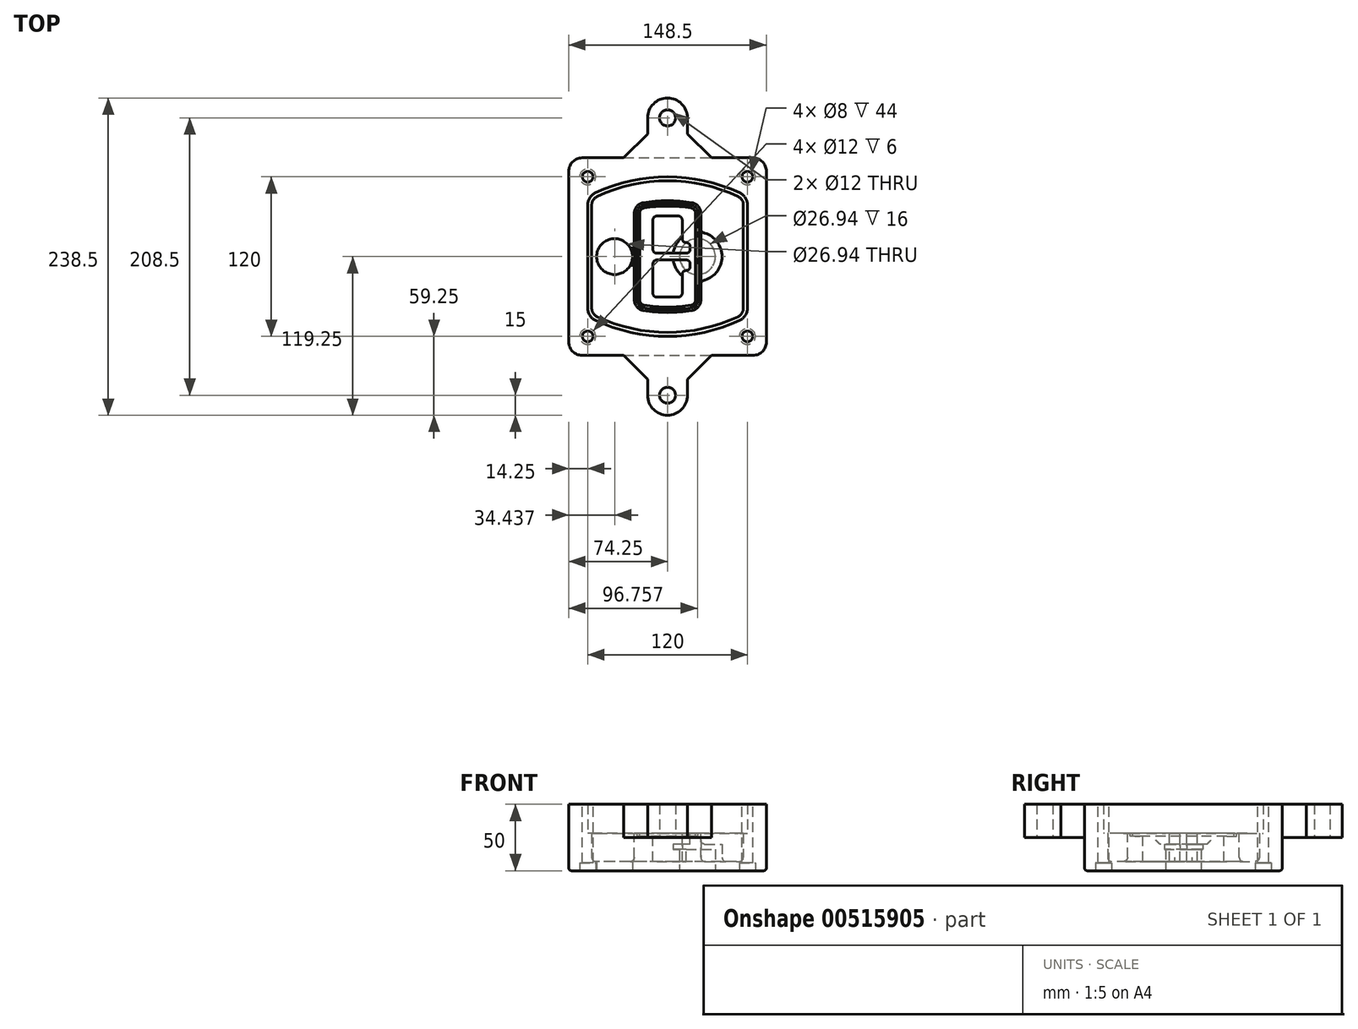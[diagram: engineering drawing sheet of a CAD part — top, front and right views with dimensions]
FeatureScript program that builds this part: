
annotation { "Feature Type Name" : "Feature", "Feature Type Description" : "" }
export const myFeature = defineFeature(function(context is Context, id is Id, definition is map)
    precondition{}
    {
        {
            var Q0;
            Q0=qCreatedBy(makeId("Top.planeOp"),FACE);
            var sketch = newSketch(context, id + "F0", { "sketchPlane" : qUnion([Q0])});
            skPoint(sketch, "E0.rect.middle", {"position": v(0, 0) * mm});
            skLineSegment(sketch, "E1.bottom", {"start": v(-64.25, -74.25) * mm, "end": v(64.25, -74.25) * mm});
            skLineSegment(sketch, "E1.top", {"start": v(-64.25, 74.25) * mm, "end": v(64.25, 74.25) * mm});
            skLineSegment(sketch, "E1.left", {"start": v(-74.25, -64.25) * mm, "end": v(-74.25, 64.25) * mm});
            skLineSegment(sketch, "E1.right", {"start": v(74.25, -64.25) * mm, "end": v(74.25, 64.25) * mm});
            skLineSegment(sketch, "E2", {"start": v(-74.25, 74.25) * mm, "end": v(74.25, -74.25) * mm, "construction": true});
            skLineSegment(sketch, "E3", {"start": v(74.25, 74.25) * mm, "end": v(-74.25, -74.25) * mm, "construction": true});
            skCircle(sketch, "E4", {"center": v(-60, 60) * mm, "radius": 4 * mm});
            skCircle(sketch, "E5", {"center": v(60, 60) * mm, "radius": 4 * mm});
            skCircle(sketch, "E6", {"center": v(60, -60) * mm, "radius": 4 * mm});
            skCircle(sketch, "E7", {"center": v(-60, -60) * mm, "radius": 4 * mm});
            skLineSegment(sketch, "E8", {"start": v(-60, 60) * mm, "end": v(60, 60) * mm, "construction": true});
            skLineSegment(sketch, "E9", {"start": v(60, 60) * mm, "end": v(60, -60) * mm, "construction": true});
            skLineSegment(sketch, "E10", {"start": v(60, -60) * mm, "end": v(-60, -60) * mm, "construction": true});
            skLineSegment(sketch, "E11", {"start": v(-60, -60) * mm, "end": v(-60, 60) * mm, "construction": true});
            skLineSegment(sketch, "E12", {"start": v(-60, 38.83) * mm, "end": v(-60, -38.83) * mm});
            skLineSegment(sketch, "E13", {"start": v(60, 38.83) * mm, "end": v(60, -38.83) * mm});
            skArc(sketch, "E14", {"start": v(54.26, 47.88) * mm, "mid": v(0, 60) * mm, "end": v(-54.26, 47.88) * mm});
            skArc(sketch, "E15", {"start": v(-54.26, -47.88) * mm, "mid": v(0, -60) * mm, "end": v(54.26, -47.88) * mm});
            skLineSegment(sketch, "E16", {"start": v(-60, 0) * mm, "end": v(60, 0) * mm, "construction": true});
            skPoint(sketch, "E17.visualSharp", {"position": v(-60, -45) * mm});
            skArc(sketch, "E17.filletArc", {"start": v(-60, -38.83) * mm, "mid": v(-58.44, -44.2) * mm, "end": v(-54.26, -47.88) * mm});
            skPoint(sketch, "E18.visualSharp", {"position": v(-60, 45) * mm});
            skArc(sketch, "E18.filletArc", {"start": v(-54.26, 47.88) * mm, "mid": v(-58.44, 44.2) * mm, "end": v(-60, 38.83) * mm});
            skPoint(sketch, "E19.visualSharp", {"position": v(60, 45) * mm});
            skArc(sketch, "E19.filletArc", {"start": v(60, 38.83) * mm, "mid": v(58.44, 44.2) * mm, "end": v(54.26, 47.88) * mm});
            skPoint(sketch, "E20.visualSharp", {"position": v(60, -45) * mm});
            skArc(sketch, "E20.filletArc", {"start": v(54.26, -47.88) * mm, "mid": v(58.44, -44.2) * mm, "end": v(60, -38.83) * mm});
            skPoint(sketch, "E21.visualSharp", {"position": v(-74.25, 74.25) * mm});
            skArc(sketch, "E21.filletArc", {"start": v(-64.25, 74.25) * mm, "mid": v(-71.32, 71.32) * mm, "end": v(-74.25, 64.25) * mm});
            skPoint(sketch, "E22.visualSharp", {"position": v(74.25, 74.25) * mm});
            skArc(sketch, "E22.filletArc", {"start": v(74.25, 64.25) * mm, "mid": v(71.32, 71.32) * mm, "end": v(64.25, 74.25) * mm});
            skPoint(sketch, "E23.visualSharp", {"position": v(74.25, -74.25) * mm});
            skArc(sketch, "E23.filletArc", {"start": v(64.25, -74.25) * mm, "mid": v(71.32, -71.32) * mm, "end": v(74.25, -64.25) * mm});
            skPoint(sketch, "E24.visualSharp", {"position": v(-74.25, -74.25) * mm});
            skArc(sketch, "E24.filletArc", {"start": v(-74.25, -64.25) * mm, "mid": v(-71.32, -71.32) * mm, "end": v(-64.25, -74.25) * mm});
            skArc(sketch, "E25.0", {"start": v(57, 38.83) * mm, "mid": v(55.9, 42.58) * mm, "end": v(52.98, 45.17) * mm});
            skLineSegment(sketch, "E25.1", {"start": v(57, 38.83) * mm, "end": v(57, -38.83) * mm});
            skArc(sketch, "E25.2", {"start": v(52.98, -45.17) * mm, "mid": v(55.9, -42.58) * mm, "end": v(57, -38.83) * mm});
            skArc(sketch, "E25.3", {"start": v(-52.98, -45.17) * mm, "mid": v(0, -57) * mm, "end": v(52.98, -45.17) * mm});
            skArc(sketch, "E25.4", {"start": v(-57, -38.83) * mm, "mid": v(-55.9, -42.58) * mm, "end": v(-52.98, -45.17) * mm});
            skArc(sketch, "E25.5", {"start": v(52.98, 45.17) * mm, "mid": v(0, 57) * mm, "end": v(-52.98, 45.17) * mm});
            skLineSegment(sketch, "E25.6", {"start": v(-57, 38.83) * mm, "end": v(-57, -38.83) * mm});
            skArc(sketch, "E25.7", {"start": v(-52.98, 45.17) * mm, "mid": v(-55.9, 42.58) * mm, "end": v(-57, 38.83) * mm});
            skArc(sketch, "E26.0", {"start": v(-55.96, 51.5) * mm, "mid": v(-61.82, 46.33) * mm, "end": v(-64, 38.83) * mm});
            skArc(sketch, "E26.1", {"start": v(55.96, 51.5) * mm, "mid": v(0, 64) * mm, "end": v(-55.96, 51.5) * mm});
            skArc(sketch, "E26.2", {"start": v(64, 38.83) * mm, "mid": v(61.82, 46.33) * mm, "end": v(55.96, 51.5) * mm});
            skLineSegment(sketch, "E26.3", {"start": v(64, 38.83) * mm, "end": v(64, -38.83) * mm});
            skArc(sketch, "E26.4", {"start": v(55.96, -51.5) * mm, "mid": v(61.82, -46.33) * mm, "end": v(64, -38.83) * mm});
            skLineSegment(sketch, "E26.5", {"start": v(-64, 38.83) * mm, "end": v(-64, -38.83) * mm});
            skArc(sketch, "E26.6", {"start": v(-55.96, -51.5) * mm, "mid": v(0, -64) * mm, "end": v(55.96, -51.5) * mm});
            skArc(sketch, "E26.7", {"start": v(-64, -38.83) * mm, "mid": v(-61.82, -46.33) * mm, "end": v(-55.96, -51.5) * mm});
            skSolve(sketch);
        }
        {
            var Q0;
            Q0=makeQuery(id+"F0.imprint","IMPRINT",FACE,{"disambiguationData":[TD([[makeQuery(id+"F0.imprint","IMPRINT",EDGE,{"derivedFrom":sQuery(id+"F0.wireOp",EDGE,"E1.bottom")}),1.0]])]});
            var Q1;
            Q1=makeQuery(id+"F0.imprint","IMPRINT",FACE,{"disambiguationData":[TD([[makeQuery(id+"F0.imprint","IMPRINT",EDGE,{"derivedFrom":sQuery(id+"F0.wireOp",EDGE,"E12")}),1.0]])]});
            var Q2;
            Q2=makeQuery(id+"F0.imprint","IMPRINT",FACE,{"disambiguationData":[TD([[makeQuery(id+"F0.imprint","IMPRINT",EDGE,{"derivedFrom":sQuery(id+"F0.wireOp",EDGE,"E25.0")}),1.0]])]});
            var Q3;
            Q3=makeQuery(id+"F0.imprint","IMPRINT",FACE,{"disambiguationData":[TD([[makeQuery(id+"F0.imprint","IMPRINT",EDGE,{"derivedFrom":sQuery(id+"F0.wireOp",EDGE,"E12")}),-1.0]])]});
            extrude(context, id + "F1", {"entities" : qUnion([Q0, Q1, Q2, Q3]), "oppositeDirection" : true, "depth" : 25 * mm});
        }
        {
            var Q0;
            Q0=makeQuery(id+"F0.imprint","IMPRINT",FACE,{"disambiguationData":[TD([[makeQuery(id+"F0.imprint","IMPRINT",EDGE,{"derivedFrom":sQuery(id+"F0.wireOp",EDGE,"E12")}),1.0]])]});
            extrude(context, id + "F2", {"entities" : qUnion([Q0]), "operationType" : NewBodyOperationType.ADD, "depth" : 3 * mm});
        }
        {
            var Q0;
            Q0=makeQuery(id+"F0.imprint","IMPRINT",FACE,{"disambiguationData":[TD([[makeQuery(id+"F0.imprint","IMPRINT",EDGE,{"derivedFrom":sQuery(id+"F0.wireOp",EDGE,"E25.0")}),1.0]])]});
            extrude(context, id + "F3", {"entities" : qUnion([Q0]), "operationType" : NewBodyOperationType.REMOVE, "oppositeDirection" : true, "depth" : 18 * mm});
        }
        {
            var Q0;
            Q0=makeQuery(id+"F2.opExtrude","CAP_FACE",FACE,{"disambiguationData":[OSD([sQuery(id+"F0.wireOp",EDGE,"E12"),sQuery(id+"F0.wireOp",EDGE,"E13"),sQuery(id+"F0.wireOp",EDGE,"E14"),sQuery(id+"F0.wireOp",EDGE,"E15"),sQuery(id+"F0.wireOp",EDGE,"E17.filletArc"),sQuery(id+"F0.wireOp",EDGE,"E18.filletArc"),sQuery(id+"F0.wireOp",EDGE,"E19.filletArc"),sQuery(id+"F0.wireOp",EDGE,"E20.filletArc"),sQuery(id+"F0.wireOp",EDGE,"E25.0"),sQuery(id+"F0.wireOp",EDGE,"E25.1"),sQuery(id+"F0.wireOp",EDGE,"E25.2"),sQuery(id+"F0.wireOp",EDGE,"E25.3"),sQuery(id+"F0.wireOp",EDGE,"E25.4"),sQuery(id+"F0.wireOp",EDGE,"E25.5"),sQuery(id+"F0.wireOp",EDGE,"E25.6"),sQuery(id+"F0.wireOp",EDGE,"E25.7")])],"isStart":false});
            var sketch = newSketch(context, id + "F4", { "sketchPlane" : qUnion([Q0])});
            skArc(sketch, "E27.0", {"start": v(-18.34, -40.45) * mm, "mid": v(0, -42) * mm, "end": v(18.34, -40.45) * mm});
            skArc(sketch, "E28.0", {"start": v(18.34, 40.45) * mm, "mid": v(0, 42) * mm, "end": v(-18.34, 40.45) * mm});
            skLineSegment(sketch, "E29", {"start": v(-25, 32.57) * mm, "end": v(-25, -32.57) * mm});
            skLineSegment(sketch, "E30", {"start": v(25, 32.57) * mm, "end": v(25, -32.57) * mm});
            skLineSegment(sketch, "E31", {"start": v(-25, 39.1) * mm, "end": v(25, 39.1) * mm, "construction": true});
            skLineSegment(sketch, "E32", {"start": v(-25, -39.1) * mm, "end": v(25, -39.1) * mm, "construction": true});
            skPoint(sketch, "E33.visualSharp", {"position": v(-25, 39.1) * mm});
            skArc(sketch, "E33.filletArc", {"start": v(-18.34, 40.45) * mm, "mid": v(-23.11, 37.73) * mm, "end": v(-25, 32.57) * mm});
            skPoint(sketch, "E34.visualSharp", {"position": v(25, 39.1) * mm});
            skArc(sketch, "E34.filletArc", {"start": v(25, 32.57) * mm, "mid": v(23.11, 37.73) * mm, "end": v(18.34, 40.45) * mm});
            skPoint(sketch, "E35.visualSharp", {"position": v(25, -39.1) * mm});
            skArc(sketch, "E35.filletArc", {"start": v(18.34, -40.45) * mm, "mid": v(23.11, -37.73) * mm, "end": v(25, -32.57) * mm});
            skPoint(sketch, "E36.visualSharp", {"position": v(-25, -39.1) * mm});
            skArc(sketch, "E36.filletArc", {"start": v(-25, -32.57) * mm, "mid": v(-23.11, -37.73) * mm, "end": v(-18.34, -40.45) * mm});
            skArc(sketch, "E37.0", {"start": v(52.98, 45.17) * mm, "mid": v(0, 57) * mm, "end": v(-52.98, 45.17) * mm});
            skArc(sketch, "E37.1", {"start": v(-52.98, 45.17) * mm, "mid": v(-55.9, 42.58) * mm, "end": v(-57, 38.83) * mm});
            skLineSegment(sketch, "E37.2", {"start": v(-57, 38.83) * mm, "end": v(-57, -38.83) * mm});
            skArc(sketch, "E37.3", {"start": v(-57, -38.83) * mm, "mid": v(-55.9, -42.58) * mm, "end": v(-52.98, -45.17) * mm});
            skArc(sketch, "E37.4", {"start": v(-52.98, -45.17) * mm, "mid": v(0, -57) * mm, "end": v(52.98, -45.17) * mm});
            skArc(sketch, "E37.5", {"start": v(52.98, -45.17) * mm, "mid": v(55.9, -42.58) * mm, "end": v(57, -38.83) * mm});
            skLineSegment(sketch, "E37.6", {"start": v(57, 38.83) * mm, "end": v(57, -38.83) * mm});
            skArc(sketch, "E37.7", {"start": v(57, 38.83) * mm, "mid": v(55.9, 42.58) * mm, "end": v(52.98, 45.17) * mm});
            skLineSegment(sketch, "E38.0", {"start": v(23, 32.57) * mm, "end": v(23, -32.57) * mm});
            skArc(sketch, "E38.1", {"start": v(18, -38.48) * mm, "mid": v(21.58, -36.44) * mm, "end": v(23, -32.57) * mm});
            skArc(sketch, "E38.2", {"start": v(-18, -38.48) * mm, "mid": v(0, -40) * mm, "end": v(18, -38.48) * mm});
            skArc(sketch, "E38.3", {"start": v(-23, -32.57) * mm, "mid": v(-21.58, -36.44) * mm, "end": v(-18, -38.48) * mm});
            skLineSegment(sketch, "E38.4", {"start": v(-23, 32.57) * mm, "end": v(-23, -32.57) * mm});
            skArc(sketch, "E38.5", {"start": v(23, 32.57) * mm, "mid": v(21.58, 36.44) * mm, "end": v(18, 38.48) * mm});
            skArc(sketch, "E38.6", {"start": v(-18, 38.48) * mm, "mid": v(-21.58, 36.44) * mm, "end": v(-23, 32.57) * mm});
            skArc(sketch, "E38.7", {"start": v(18, 38.48) * mm, "mid": v(0, 40) * mm, "end": v(-18, 38.48) * mm});
            skArc(sketch, "E39.0", {"start": v(21, 32.57) * mm, "mid": v(20.06, 35.15) * mm, "end": v(17.67, 36.5) * mm});
            skLineSegment(sketch, "E39.1", {"start": v(21, 32.57) * mm, "end": v(21, -32.57) * mm});
            skArc(sketch, "E39.2", {"start": v(17.67, -36.5) * mm, "mid": v(20.06, -35.15) * mm, "end": v(21, -32.57) * mm});
            skArc(sketch, "E39.3", {"start": v(-17.67, -36.5) * mm, "mid": v(0, -38) * mm, "end": v(17.67, -36.5) * mm});
            skArc(sketch, "E39.4", {"start": v(-21, -32.57) * mm, "mid": v(-20.06, -35.15) * mm, "end": v(-17.67, -36.5) * mm});
            skArc(sketch, "E39.5", {"start": v(17.67, 36.5) * mm, "mid": v(0, 38) * mm, "end": v(-17.67, 36.5) * mm});
            skLineSegment(sketch, "E39.6", {"start": v(-21, 32.57) * mm, "end": v(-21, -32.57) * mm});
            skArc(sketch, "E39.7", {"start": v(-17.67, 36.5) * mm, "mid": v(-20.06, 35.15) * mm, "end": v(-21, 32.57) * mm});
            skLineSegment(sketch, "E40", {"start": v(-25, 0) * mm, "end": v(25, 0) * mm, "construction": true});
            skLineSegment(sketch, "E41", {"start": v(-11, 5.5) * mm, "end": v(-11, 27.5) * mm});
            skLineSegment(sketch, "E42", {"start": v(-8, 30.5) * mm, "end": v(8, 30.5) * mm});
            skLineSegment(sketch, "E43", {"start": v(11, 27.5) * mm, "end": v(11, 13.5) * mm});
            skLineSegment(sketch, "E44", {"start": v(14, 10.5) * mm, "end": v(14, 10.5) * mm});
            skLineSegment(sketch, "E45", {"start": v(17, 7.5) * mm, "end": v(17, 5.5) * mm});
            skLineSegment(sketch, "E46", {"start": v(14, 2.5) * mm, "end": v(-8, 2.5) * mm});
            skPoint(sketch, "E47.visualSharp", {"position": v(-11, 30.5) * mm});
            skArc(sketch, "E47.filletArc", {"start": v(-8, 30.5) * mm, "mid": v(-10.12, 29.62) * mm, "end": v(-11, 27.5) * mm});
            skPoint(sketch, "E48.visualSharp", {"position": v(11, 30.5) * mm});
            skArc(sketch, "E48.filletArc", {"start": v(11, 27.5) * mm, "mid": v(10.12, 29.62) * mm, "end": v(8, 30.5) * mm});
            skPoint(sketch, "E49.visualSharp", {"position": v(11, 10.5) * mm});
            skArc(sketch, "E49.filletArc", {"start": v(11, 13.5) * mm, "mid": v(11.88, 11.38) * mm, "end": v(14, 10.5) * mm});
            skPoint(sketch, "E50.visualSharp", {"position": v(17, 10.5) * mm});
            skArc(sketch, "E50.filletArc", {"start": v(17, 7.5) * mm, "mid": v(16.12, 9.62) * mm, "end": v(14, 10.5) * mm});
            skPoint(sketch, "E51.visualSharp", {"position": v(17, 2.5) * mm});
            skArc(sketch, "E51.filletArc", {"start": v(14, 2.5) * mm, "mid": v(16.12, 3.38) * mm, "end": v(17, 5.5) * mm});
            skPoint(sketch, "E52.visualSharp", {"position": v(-11, 2.5) * mm});
            skArc(sketch, "E52.filletArc", {"start": v(-11, 5.5) * mm, "mid": v(-10.12, 3.38) * mm, "end": v(-8, 2.5) * mm});
            skLineSegment(sketch, "E53.0.MirrorCS", {"start": v(14, -2.5) * mm, "end": v(-8, -2.5) * mm});
            skArc(sketch, "E54.0.MirrorCS", {"start": v(-11, -5.5) * mm, "mid": v(-10.12, -3.38) * mm, "end": v(-8, -2.5) * mm});
            skLineSegment(sketch, "E55.0.MirrorCS", {"start": v(-11, -5.5) * mm, "end": v(-11, -27.5) * mm});
            skArc(sketch, "E56.0.MirrorCS", {"start": v(-8, -30.5) * mm, "mid": v(-10.12, -29.62) * mm, "end": v(-11, -27.5) * mm});
            skLineSegment(sketch, "E57.0.MirrorCS", {"start": v(-8, -30.5) * mm, "end": v(8, -30.5) * mm});
            skArc(sketch, "E58.0.MirrorCS", {"start": v(11, -27.5) * mm, "mid": v(10.12, -29.62) * mm, "end": v(8, -30.5) * mm});
            skLineSegment(sketch, "E59.0.MirrorCS", {"start": v(11, -27.5) * mm, "end": v(11, -13.5) * mm});
            skArc(sketch, "E60.0.MirrorCS", {"start": v(11, -13.5) * mm, "mid": v(11.88, -11.38) * mm, "end": v(14, -10.5) * mm});
            skArc(sketch, "E61.0.MirrorCS", {"start": v(17, -7.5) * mm, "mid": v(16.12, -9.62) * mm, "end": v(14, -10.5) * mm});
            skLineSegment(sketch, "E62.0.MirrorCS", {"start": v(17, -7.5) * mm, "end": v(17, -5.5) * mm});
            skArc(sketch, "E63.0.MirrorCS", {"start": v(14, -2.5) * mm, "mid": v(16.12, -3.38) * mm, "end": v(17, -5.5) * mm});
            skSolve(sketch);
        }
        {
            var Q0;
            Q0=makeQuery(id+"F4.imprint","IMPRINT",FACE,{"disambiguationData":[TD([[makeQuery(id+"F4.imprint","IMPRINT",EDGE,{"derivedFrom":sQuery(id+"F4.wireOp",EDGE,"E27.0")}),1.0]])]});
            var Q1;
            Q1=makeQuery(id+"F4.imprint","IMPRINT",FACE,{"disambiguationData":[TD([[makeQuery(id+"F4.imprint","IMPRINT",EDGE,{"derivedFrom":sQuery(id+"F4.wireOp",EDGE,"E38.0")}),-1.0]])]});
            var Q2;
            Q2=makeQuery(id+"F4.imprint","IMPRINT",FACE,{"disambiguationData":[TD([[makeQuery(id+"F4.imprint","IMPRINT",EDGE,{"derivedFrom":sQuery(id+"F4.wireOp",EDGE,"E39.0")}),1.0]])]});
            extrude(context, id + "F5", {"entities" : qUnion([Q0, Q1, Q2]), "operationType" : NewBodyOperationType.ADD, "endBound" : BoundingType.UP_TO_NEXT, "oppositeDirection" : true, "depth" : 25 * mm});
        }
        {
            var Q0;
            Q0=makeQuery(id+"F4.imprint","IMPRINT",FACE,{"disambiguationData":[TD([[makeQuery(id+"F4.imprint","IMPRINT",EDGE,{"derivedFrom":sQuery(id+"F4.wireOp",EDGE,"E38.0")}),-1.0]])]});
            extrude(context, id + "F6", {"entities" : qUnion([Q0]), "operationType" : NewBodyOperationType.REMOVE, "oppositeDirection" : true, "depth" : 2 * mm});
        }
        {
            var Q0;
            Q0=makeQuery(id+"F1.opExtrude","CAP_FACE",FACE,{"disambiguationData":[OSD([sQuery(id+"F0.wireOp",EDGE,"E1.bottom"),sQuery(id+"F0.wireOp",EDGE,"E1.top"),sQuery(id+"F0.wireOp",EDGE,"E1.left"),sQuery(id+"F0.wireOp",EDGE,"E1.right"),sQuery(id+"F0.wireOp",EDGE,"E4"),sQuery(id+"F0.wireOp",EDGE,"E5"),sQuery(id+"F0.wireOp",EDGE,"E6"),sQuery(id+"F0.wireOp",EDGE,"E7"),sQuery(id+"F0.wireOp",EDGE,"E21.filletArc"),sQuery(id+"F0.wireOp",EDGE,"E22.filletArc"),sQuery(id+"F0.wireOp",EDGE,"E23.filletArc"),sQuery(id+"F0.wireOp",EDGE,"E24.filletArc")])],"isStart":false});
            var sketch = newSketch(context, id + "F7", { "sketchPlane" : qUnion([Q0])});
            skCircle(sketch, "E64", {"center": v(22.5, 0) * mm, "radius": 13.47 * mm});
            skCircle(sketch, "E65", {"center": v(-39.81, 0) * mm, "radius": 13.47 * mm});
            skLineSegment(sketch, "E66", {"start": v(74.25, 0) * mm, "end": v(-74.25, 0) * mm});
            skCircle(sketch, "E67", {"center": v(22.5, 0) * mm, "radius": 18.47 * mm});
            skCircle(sketch, "E68", {"center": v(60, -60) * mm, "radius": 6 * mm});
            skCircle(sketch, "E69", {"center": v(-60, -60) * mm, "radius": 6 * mm});
            skCircle(sketch, "E70", {"center": v(-60, 60) * mm, "radius": 6 * mm});
            skCircle(sketch, "E71", {"center": v(60, 60) * mm, "radius": 6 * mm});
            skSolve(sketch);
        }
        {
            var Q0;
            {var subQ1=sQuery(id+"F7.wireOp",EDGE,"E66");var subQ4=sQuery(id+"F7.wireOp",EDGE,"E64");var subQ6=makeQuery(id+"F7.imprint","INTERSECT",VERTEX,{"disambiguationData":[OD(0.0)],"derivedFrom":[subQ4,subQ1]});Q0=makeQuery(id+"F7.imprint","IMPRINT",FACE,{"disambiguationData":[TD([[makeQuery(id+"F7.imprint","IMPRINT",EDGE,{"disambiguationData":[TD([[subQ6,-1.0]])],"derivedFrom":subQ4}),-1.0]])]});}
            var Q1;
            {var subQ0=sQuery(id+"F7.wireOp",EDGE,"E66");var subQ1=sQuery(id+"F7.wireOp",EDGE,"E64");var subQ3=makeQuery(id+"F7.imprint","INTERSECT",VERTEX,{"disambiguationData":[OD(0.0)],"derivedFrom":[subQ1,subQ0]});Q1=makeQuery(id+"F7.imprint","IMPRINT",FACE,{"disambiguationData":[TD([[makeQuery(id+"F7.imprint","IMPRINT",EDGE,{"disambiguationData":[TD([[subQ3,-1.0]])],"derivedFrom":subQ1}),1.0]])]});}
            var Q2;
            {var subQ0=sQuery(id+"F7.wireOp",EDGE,"E66");var subQ1=sQuery(id+"F7.wireOp",EDGE,"E64");var subQ3=makeQuery(id+"F7.imprint","INTERSECT",VERTEX,{"disambiguationData":[OD(0.0)],"derivedFrom":[subQ1,subQ0]});Q2=makeQuery(id+"F7.imprint","IMPRINT",FACE,{"disambiguationData":[TD([[makeQuery(id+"F7.imprint","IMPRINT",EDGE,{"disambiguationData":[TD([[subQ3,1.0]])],"derivedFrom":subQ1}),1.0]])]});}
            var Q3;
            {var subQ1=sQuery(id+"F7.wireOp",EDGE,"E66");var subQ4=sQuery(id+"F7.wireOp",EDGE,"E64");var subQ6=makeQuery(id+"F7.imprint","INTERSECT",VERTEX,{"disambiguationData":[OD(0.0)],"derivedFrom":[subQ4,subQ1]});Q3=makeQuery(id+"F7.imprint","IMPRINT",FACE,{"disambiguationData":[TD([[makeQuery(id+"F7.imprint","IMPRINT",EDGE,{"disambiguationData":[TD([[subQ6,1.0]])],"derivedFrom":subQ4}),-1.0]])]});}
            extrude(context, id + "F8", {"entities" : qUnion([Q0, Q1, Q2, Q3]), "operationType" : NewBodyOperationType.ADD, "oppositeDirection" : true, "depth" : 20 * mm});
        }
        {
            var Q0;
            {var subQ0=sQuery(id+"F7.wireOp",EDGE,"E66");var subQ1=sQuery(id+"F7.wireOp",EDGE,"E64");var subQ3=makeQuery(id+"F7.imprint","INTERSECT",VERTEX,{"disambiguationData":[OD(0.0)],"derivedFrom":[subQ1,subQ0]});Q0=makeQuery(id+"F7.imprint","IMPRINT",FACE,{"disambiguationData":[TD([[makeQuery(id+"F7.imprint","IMPRINT",EDGE,{"disambiguationData":[TD([[subQ3,-1.0]])],"derivedFrom":subQ1}),1.0]])]});}
            var Q1;
            {var subQ0=sQuery(id+"F7.wireOp",EDGE,"E66");var subQ1=sQuery(id+"F7.wireOp",EDGE,"E64");var subQ3=makeQuery(id+"F7.imprint","INTERSECT",VERTEX,{"disambiguationData":[OD(0.0)],"derivedFrom":[subQ1,subQ0]});Q1=makeQuery(id+"F7.imprint","IMPRINT",FACE,{"disambiguationData":[TD([[makeQuery(id+"F7.imprint","IMPRINT",EDGE,{"disambiguationData":[TD([[subQ3,1.0]])],"derivedFrom":subQ1}),1.0]])]});}
            extrude(context, id + "F9", {"entities" : qUnion([Q0, Q1]), "operationType" : NewBodyOperationType.REMOVE, "oppositeDirection" : true, "depth" : 16 * mm});
        }
        {
            var Q0;
            {var subQ0=sQuery(id+"F7.wireOp",EDGE,"E66");var subQ1=sQuery(id+"F7.wireOp",EDGE,"E65");var subQ3=makeQuery(id+"F7.imprint","INTERSECT",VERTEX,{"disambiguationData":[OD(0.0)],"derivedFrom":[subQ1,subQ0]});Q0=makeQuery(id+"F7.imprint","IMPRINT",FACE,{"disambiguationData":[TD([[makeQuery(id+"F7.imprint","IMPRINT",EDGE,{"disambiguationData":[TD([[subQ3,-1.0]])],"derivedFrom":subQ1}),1.0]])]});}
            var Q1;
            {var subQ0=sQuery(id+"F7.wireOp",EDGE,"E66");var subQ1=sQuery(id+"F7.wireOp",EDGE,"E65");var subQ3=makeQuery(id+"F7.imprint","INTERSECT",VERTEX,{"disambiguationData":[OD(0.0)],"derivedFrom":[subQ1,subQ0]});Q1=makeQuery(id+"F7.imprint","IMPRINT",FACE,{"disambiguationData":[TD([[makeQuery(id+"F7.imprint","IMPRINT",EDGE,{"disambiguationData":[TD([[subQ3,1.0]])],"derivedFrom":subQ1}),1.0]])]});}
            extrude(context, id + "F10", {"entities" : qUnion([Q0, Q1]), "operationType" : NewBodyOperationType.REMOVE, "oppositeDirection" : true, "depth" : 25 * mm});
        }
        {
            var Q0;
            Q0=makeQuery(id+"F7.imprint","IMPRINT",FACE,{"disambiguationData":[TD([[makeQuery(id+"F7.imprint","IMPRINT",EDGE,{"derivedFrom":sQuery(id+"F7.wireOp",EDGE,"E68")}),1.0]])]});
            var Q1;
            Q1=makeQuery(id+"F7.imprint","IMPRINT",FACE,{"disambiguationData":[TD([[makeQuery(id+"F7.imprint","IMPRINT",EDGE,{"derivedFrom":makeQuery(id+"F1.opExtrude","CAP_EDGE",EDGE,{"disambiguationData":[OSD([sQuery(id+"F0.wireOp",EDGE,"E5")])],"isStart":false})}),-1.0]])]});
            var Q2;
            Q2=makeQuery(id+"F7.imprint","IMPRINT",FACE,{"disambiguationData":[TD([[makeQuery(id+"F7.imprint","IMPRINT",EDGE,{"derivedFrom":sQuery(id+"F7.wireOp",EDGE,"E69")}),1.0]])]});
            var Q3;
            Q3=makeQuery(id+"F7.imprint","IMPRINT",FACE,{"disambiguationData":[TD([[makeQuery(id+"F7.imprint","IMPRINT",EDGE,{"derivedFrom":makeQuery(id+"F1.opExtrude","CAP_EDGE",EDGE,{"disambiguationData":[OSD([sQuery(id+"F0.wireOp",EDGE,"E4")])],"isStart":false})}),-1.0]])]});
            var Q4;
            Q4=makeQuery(id+"F7.imprint","IMPRINT",FACE,{"disambiguationData":[TD([[makeQuery(id+"F7.imprint","IMPRINT",EDGE,{"derivedFrom":sQuery(id+"F7.wireOp",EDGE,"E70")}),1.0]])]});
            var Q5;
            Q5=makeQuery(id+"F7.imprint","IMPRINT",FACE,{"disambiguationData":[TD([[makeQuery(id+"F7.imprint","IMPRINT",EDGE,{"derivedFrom":makeQuery(id+"F1.opExtrude","CAP_EDGE",EDGE,{"disambiguationData":[OSD([sQuery(id+"F0.wireOp",EDGE,"E7")])],"isStart":false})}),-1.0]])]});
            var Q6;
            Q6=makeQuery(id+"F7.imprint","IMPRINT",FACE,{"disambiguationData":[TD([[makeQuery(id+"F7.imprint","IMPRINT",EDGE,{"derivedFrom":sQuery(id+"F7.wireOp",EDGE,"E71")}),1.0]])]});
            var Q7;
            Q7=makeQuery(id+"F7.imprint","IMPRINT",FACE,{"disambiguationData":[TD([[makeQuery(id+"F7.imprint","IMPRINT",EDGE,{"derivedFrom":makeQuery(id+"F1.opExtrude","CAP_EDGE",EDGE,{"disambiguationData":[OSD([sQuery(id+"F0.wireOp",EDGE,"E6")])],"isStart":false})}),-1.0]])]});
            extrude(context, id + "F11", {"entities" : qUnion([Q0, Q1, Q2, Q3, Q4, Q5, Q6, Q7]), "operationType" : NewBodyOperationType.REMOVE, "oppositeDirection" : true, "depth" : 6 * mm});
        }
        {
            var Q0;
            Q0=makeQuery(id+"F9.boolean.opBoolean","COPY",FACE,{"derivedFrom":makeQuery(id+"F9.opExtrude","CAP_FACE",FACE,{"disambiguationData":[OSD([sQuery(id+"F7.wireOp",EDGE,"E64")])],"isStart":false})});
            var sketch = newSketch(context, id + "F12", { "sketchPlane" : qUnion([Q0])});
            skArc(sketch, "E72.0", {"start": v(11, 14.45) * mm, "mid": v(6.45, 9.13) * mm, "end": v(4.2, 2.5) * mm});
            skArc(sketch, "E72.1", {"start": v(4.2, -2.5) * mm, "mid": v(6.45, -9.13) * mm, "end": v(11, -14.45) * mm});
            skLineSegment(sketch, "E73", {"start": v(4.2, -2.5) * mm, "end": v(14, -2.5) * mm});
            skLineSegment(sketch, "E74.0", {"start": v(14, 2.5) * mm, "end": v(4.2, 2.5) * mm});
            skArc(sketch, "E74.1", {"start": v(14, 2.5) * mm, "mid": v(16.12, 3.38) * mm, "end": v(17, 5.5) * mm});
            skLineSegment(sketch, "E74.2", {"start": v(17, 7.5) * mm, "end": v(17, 5.5) * mm});
            skArc(sketch, "E74.3", {"start": v(17, 7.5) * mm, "mid": v(16.12, 9.62) * mm, "end": v(14, 10.5) * mm});
            skArc(sketch, "E74.4", {"start": v(11, 13.5) * mm, "mid": v(11.88, 11.38) * mm, "end": v(14, 10.5) * mm});
            skLineSegment(sketch, "E74.5", {"start": v(11, 14.45) * mm, "end": v(11, 13.5) * mm});
            skLineSegment(sketch, "E74.7", {"start": v(14, -2.5) * mm, "end": v(4.2, -2.5) * mm});
            skArc(sketch, "E74.8", {"start": v(14, -2.5) * mm, "mid": v(16.12, -3.38) * mm, "end": v(17, -5.5) * mm});
            skLineSegment(sketch, "E74.9", {"start": v(17, -7.5) * mm, "end": v(17, -5.5) * mm});
            skArc(sketch, "E74.10", {"start": v(17, -7.5) * mm, "mid": v(16.12, -9.62) * mm, "end": v(14, -10.5) * mm});
            skArc(sketch, "E74.11", {"start": v(11, -13.5) * mm, "mid": v(11.88, -11.38) * mm, "end": v(14, -10.5) * mm});
            skLineSegment(sketch, "E74.12", {"start": v(11, -14.45) * mm, "end": v(11, -13.5) * mm});
            skPoint(sketch, "E75.orphan", {"position": v(11, -27.5) * mm});
            skPoint(sketch, "E76.orphan", {"position": v(-8, -2.5) * mm});
            skPoint(sketch, "E77.orphan", {"position": v(-8, 2.5) * mm});
            skPoint(sketch, "E78.orphan", {"position": v(11, 27.5) * mm});
            skSolve(sketch);
        }
        {
            var Q0;
            {var subQ7=sQuery(id+"F12.wireOp",EDGE,"E72.0");var subQ14=sQuery(id+"F12.wireOp",EDGE,"E72.1");var subQ16=sQuery(id+"F12.wireOp",EDGE,"E74.1");var subQ18=sQuery(id+"F12.wireOp",EDGE,"E74.8");Q0=qUnion([makeQuery(id+"F12.imprint","IMPRINT",FACE,{"disambiguationData":[TD([[makeQuery(id+"F12.imprint","IMPRINT",EDGE,{"derivedFrom":subQ7}),1.0]])]}),makeQuery(id+"F12.imprint","IMPRINT",FACE,{"disambiguationData":[TD([[makeQuery(id+"F12.imprint","IMPRINT",EDGE,{"derivedFrom":subQ14}),1.0]])]}),makeQuery(id+"F12.imprint","IMPRINT",FACE,{"disambiguationData":[TD([[makeQuery(id+"F12.imprint","IMPRINT",EDGE,{"derivedFrom":subQ16}),1.0]])]}),makeQuery(id+"F12.imprint","IMPRINT",FACE,{"disambiguationData":[TD([[makeQuery(id+"F12.imprint","IMPRINT",EDGE,{"derivedFrom":subQ18}),-1.0]])]})]);}
            var Q1;
            Q1=makeQuery(id+"F5.boolean.opBoolean","SPLIT",FACE,{"disambiguationData":[TD([makeQuery(id+"F5.opExtrude","SWEPT_FACE",FACE,{"disambiguationData":[OSD([sQuery(id+"F4.wireOp",EDGE,"E41")])]})])],"derivedFrom":makeQuery(id+"F3.boolean.opBoolean","COPY",FACE,{"derivedFrom":makeQuery(id+"F3.opExtrude","CAP_FACE",FACE,{"disambiguationData":[OSD([sQuery(id+"F0.wireOp",EDGE,"E25.0"),sQuery(id+"F0.wireOp",EDGE,"E25.1"),sQuery(id+"F0.wireOp",EDGE,"E25.2"),sQuery(id+"F0.wireOp",EDGE,"E25.3"),sQuery(id+"F0.wireOp",EDGE,"E25.4"),sQuery(id+"F0.wireOp",EDGE,"E25.5"),sQuery(id+"F0.wireOp",EDGE,"E25.6"),sQuery(id+"F0.wireOp",EDGE,"E25.7")])],"isStart":false})})});
            extrude(context, id + "F13", {"entities" : qUnion([Q0]), "operationType" : NewBodyOperationType.REMOVE, "endBound" : BoundingType.UP_TO_SURFACE, "endBoundEntityFace" : qUnion([Q1]), "depth" : 25 * mm});
        }
        {
            var Q0;
            Q0=makeQuery(id+"F3.boolean.opBoolean","COPY",EDGE,{"derivedFrom":makeQuery(id+"F3.opExtrude","CAP_EDGE",EDGE,{"disambiguationData":[OSD([sQuery(id+"F0.wireOp",EDGE,"E25.6")])],"isStart":false})});
            var Q1;
            Q1=makeQuery(id+"F8.boolean.opBoolean","INTERSECT",EDGE,{"derivedFrom":[makeQuery(id+"F5.opExtrude","SWEPT_FACE",FACE,{"disambiguationData":[OSD([sQuery(id+"F4.wireOp",EDGE,"E30")])]}),makeQuery(id+"F8.opExtrude","CAP_FACE",FACE,{"disambiguationData":[OSD([sQuery(id+"F7.wireOp",EDGE,"E67")])],"isStart":false})]});
            var Q2;
            Q2=makeQuery(id+"F8.boolean.opBoolean","INTERSECT",EDGE,{"disambiguationData":[OD(1.0)],"derivedFrom":[makeQuery(id+"F5.opExtrude","SWEPT_FACE",FACE,{"disambiguationData":[OSD([sQuery(id+"F4.wireOp",EDGE,"E30")])]}),makeQuery(id+"F8.opExtrude","SWEPT_FACE",FACE,{"disambiguationData":[OSD([sQuery(id+"F7.wireOp",EDGE,"E67")])]})]});
            var Q3;
            {var subQ0=sQuery(id+"F4.wireOp",EDGE,"E30");Q3=makeQuery(id+"F8.boolean.opBoolean","SPLIT",EDGE,{"disambiguationData":[TD([makeQuery(id+"F5.opExtrude","SWEPT_FACE",FACE,{"disambiguationData":[OSD([sQuery(id+"F4.wireOp",EDGE,"E35.filletArc")])]})])],"derivedFrom":makeQuery(id+"F5.opExtrude","CAP_EDGE",EDGE,{"disambiguationData":[OSD([subQ0])],"isStart":false})});}
            var Q4;
            {var subQ0=sQuery(id+"F0.wireOp",EDGE,"E25.7");var subQ1=sQuery(id+"F0.wireOp",EDGE,"E25.1");var subQ2=sQuery(id+"F0.wireOp",EDGE,"E25.6");var subQ3=sQuery(id+"F0.wireOp",EDGE,"E25.5");var subQ4=sQuery(id+"F0.wireOp",EDGE,"E25.4");var subQ5=sQuery(id+"F0.wireOp",EDGE,"E25.0");var subQ6=sQuery(id+"F0.wireOp",EDGE,"E25.2");var subQ7=sQuery(id+"F0.wireOp",EDGE,"E25.3");Q4=makeQuery(id+"F8.boolean.opBoolean","INTERSECT",EDGE,{"derivedFrom":[makeQuery(id+"F5.boolean.opBoolean","SPLIT",FACE,{"disambiguationData":[TD([makeQuery(id+"F2.opExtrude","SWEPT_FACE",FACE,{"disambiguationData":[OSD([subQ5])]})])],"derivedFrom":makeQuery(id+"F3.boolean.opBoolean","COPY",FACE,{"derivedFrom":makeQuery(id+"F3.opExtrude","CAP_FACE",FACE,{"disambiguationData":[OSD([subQ5,subQ1,subQ6,subQ7,subQ4,subQ3,subQ2,subQ0])],"isStart":false})})}),makeQuery(id+"F8.opExtrude","SWEPT_FACE",FACE,{"disambiguationData":[OSD([sQuery(id+"F7.wireOp",EDGE,"E67")])]})]});}
            var Q5;
            Q5=makeQuery(id+"F8.boolean.opBoolean","INTERSECT",EDGE,{"disambiguationData":[OD(0.0)],"derivedFrom":[makeQuery(id+"F5.opExtrude","SWEPT_FACE",FACE,{"disambiguationData":[OSD([sQuery(id+"F4.wireOp",EDGE,"E30")])]}),makeQuery(id+"F8.opExtrude","SWEPT_FACE",FACE,{"disambiguationData":[OSD([sQuery(id+"F7.wireOp",EDGE,"E67")])]})]});
            fillet(context, id + "F14", {"entities" : qUnion([Q0, Q1, Q2, Q3, Q4, Q5]), "radius" : 3 * mm, "tangentPropagation" : true, "allowEdgeOverflow" : false});
        }
        {
            var Q0;
            Q0=makeQuery(id+"F1.opExtrude","CAP_EDGE",EDGE,{"disambiguationData":[OSD([sQuery(id+"F0.wireOp",EDGE,"E1.bottom")])],"isStart":false});
            fillet(context, id + "F15", {"entities" : qUnion([Q0]), "radius" : 2 * mm, "tangentPropagation" : true, "allowEdgeOverflow" : false});
        }
        {
            var Q0;
            {var subQ0=sQuery(id+"F0.wireOp",EDGE,"E21.filletArc");var subQ1=sQuery(id+"F0.wireOp",EDGE,"E7");var subQ2=sQuery(id+"F0.wireOp",EDGE,"E6");var subQ3=sQuery(id+"F0.wireOp",EDGE,"E5");var subQ4=sQuery(id+"F0.wireOp",EDGE,"E4");var subQ5=sQuery(id+"F0.wireOp",EDGE,"E22.filletArc");var subQ6=sQuery(id+"F0.wireOp",EDGE,"E1.bottom");var subQ7=sQuery(id+"F0.wireOp",EDGE,"E1.right");var subQ8=sQuery(id+"F0.wireOp",EDGE,"E1.top");var subQ9=sQuery(id+"F0.wireOp",EDGE,"E1.left");var subQ10=sQuery(id+"F0.wireOp",EDGE,"E23.filletArc");var subQ11=sQuery(id+"F0.wireOp",EDGE,"E24.filletArc");Q0=makeQuery(id+"F2.boolean.opBoolean","SPLIT",FACE,{"disambiguationData":[TD([makeQuery(id+"F1.opExtrude","SWEPT_FACE",FACE,{"disambiguationData":[OSD([subQ6])]})])],"derivedFrom":makeQuery(id+"F1.opExtrude","CAP_FACE",FACE,{"disambiguationData":[OSD([subQ6,subQ8,subQ9,subQ7,subQ4,subQ3,subQ2,subQ1,subQ0,subQ5,subQ10,subQ11])],"isStart":true})});}
            var sketch = newSketch(context, id + "F16", { "sketchPlane" : qUnion([Q0])});
            skCircle(sketch, "E79", {"center": v(0, 104.25) * mm, "radius": 6 * mm});
            skPoint(sketch, "E79.centerSnap0", {"position": v(0, 74.25) * mm});
            skArc(sketch, "E80", {"start": v(15, 104.25) * mm, "mid": v(0, 119.25) * mm, "end": v(-15, 104.25) * mm});
            skLineSegment(sketch, "E81", {"start": v(-15, 104.25) * mm, "end": v(-15, 92.25) * mm});
            skLineSegment(sketch, "E82", {"start": v(-15, 92.25) * mm, "end": v(-33, 74.25) * mm});
            skLineSegment(sketch, "E83", {"start": v(15, 104.25) * mm, "end": v(15, 92.25) * mm});
            skLineSegment(sketch, "E84", {"start": v(15, 92.25) * mm, "end": v(33, 74.25) * mm});
            skLineSegment(sketch, "E85", {"start": v(0, 104.25) * mm, "end": v(0, 74.25) * mm, "construction": true});
            skLineSegment(sketch, "E86", {"start": v(-74.25, 0) * mm, "end": v(74.25, 0) * mm, "construction": true});
            skArc(sketch, "E87.MirrorCS", {"start": v(-15, 104.25) * mm, "mid": v(0, 119.25) * mm, "end": v(15, 104.25) * mm});
            skLineSegment(sketch, "E88.MirrorCS", {"start": v(15, -252.75) * mm, "end": v(15, -240.75) * mm});
            skLineSegment(sketch, "E89.MirrorCS", {"start": v(15, -92.25) * mm, "end": v(33, -74.25) * mm});
            skLineSegment(sketch, "E90.MirrorCS", {"start": v(15, -104.25) * mm, "end": v(15, -92.25) * mm});
            skArc(sketch, "E91.MirrorCS", {"start": v(-15, -104.25) * mm, "mid": v(0, -119.25) * mm, "end": v(15, -104.25) * mm});
            skLineSegment(sketch, "E92.MirrorCS", {"start": v(-15, -92.25) * mm, "end": v(-33, -74.25) * mm});
            skCircle(sketch, "E93.MirrorC", {"center": v(0, -104.25) * mm, "radius": 6 * mm});
            skLineSegment(sketch, "E94.MirrorCS", {"start": v(0, -104.25) * mm, "end": v(0, -74.25) * mm, "construction": true});
            skLineSegment(sketch, "E95.MirrorCS", {"start": v(-15, -104.25) * mm, "end": v(-15, -92.25) * mm});
            skSolve(sketch);
        }
        {
            var Q0;
            {var subQ1=sQuery(id+"F16.wireOp",EDGE,"E84");Q0=makeQuery(id+"F16.imprint","IMPRINT",FACE,{"disambiguationData":[TD([[makeQuery(id+"F16.imprint","IMPRINT",EDGE,{"derivedFrom":subQ1}),-1.0]])]});}
            var Q1;
            {var subQ1=sQuery(id+"F16.wireOp",EDGE,"E89.MirrorCS");Q1=makeQuery(id+"F16.imprint","IMPRINT",FACE,{"disambiguationData":[TD([[makeQuery(id+"F16.imprint","IMPRINT",EDGE,{"derivedFrom":subQ1}),1.0]])]});}
            var Q2;
            Q2=makeQuery(id+"F16.imprint","IMPRINT",FACE,{"disambiguationData":[TD([[makeQuery(id+"F16.imprint","IMPRINT",EDGE,{"derivedFrom":makeQuery(id+"F1.opExtrude","CAP_EDGE",EDGE,{"disambiguationData":[OSD([sQuery(id+"F0.wireOp",EDGE,"E1.left")])],"isStart":true})}),-1.0]])]});
            extrude(context, id + "F17", {"entities" : qUnion([Q0, Q1, Q2]), "operationType" : NewBodyOperationType.ADD, "depth" : 25 * mm, "offsetDistance" : 25 * mm});
        }
    });
